# Revit family: Urinal_Siphon-Top_Spud-American_Standard-Allbrook-6550
name_source: partatom
category: Plumbing Fixtures
units: mm (PartAtom-declared; Revit-internal decimal feet)

## family parameters
Cut with Voids When Loaded = No
Host = Face
OmniClass Number = 23.45.05.21.11.21
OmniClass Title = Urinals
Part Type = Normal
Room Calculation Point = No
Round Connector Dimension = Use Radius
Shared = Yes

## types (1)
- 6550.001
    ADA Compliant = Yes
    ATS URL = http://www.atsspec.com
    Assembly Code = D2010210
    CW Connection = Yes
    CWFU = 5
    Cold Water Connection Diameter = 3/4"
    Cold Water Connection Height = 11 1/2"
    Cold Water Connection Radius = 3/8"
    Cold Water Connection Width = 4 3/4"
    Default Elevation = 17"
    Description = Allbrook 0.5 - 1.0 gpf FloWise Washout Top Spud Urinal
    Finish = Vitreous China-American Standard-020-White
    Flush Rate = 0.5gpf-1.0gpf (1.9Lpf-3.8Lpf)
    HW Connection = No
    HWFU = 0
    Height = 21 1/2"
    Installation Type = Wall Mounted
    Length = 14"
    Manufacturer = American Standard
    Masterformat Number = 22 42 13.16
    Masterformat Title = Commercial Urinals
    Material = Vitreous China-American Standard-020-White
    Model = 6550.001
    Omniclass Table 23 Code = 23.45.05.21.11.21
    Omniclass Table 23 Title = Urinals
    Price = Prices may vary. Please consult Manufacturer Representative for most up-to-date price list.
    Product Documentation Link = https://www.americanstandard-us.com
    Product Page URL = https://www.americanstandard-us.com
    Revised Date = 03/31/2021
    Shipping Weight = 28lbs (15kg)
    URL = http://www.americanstandard-us.com
    Vent Connection = No
    WFU = 5
    Warranty Information = 1 Year Limited
    Waste Connection = Yes
    Waste Connection Diameter = 2"
    Waste Connection Height = 9 1/2"
    Waste Connection Radius = 1"
    Width = 14 5/16"

## geometry (parser evidence)
native form markers: Sweep x2
no freeform markers — native parametric forms only
